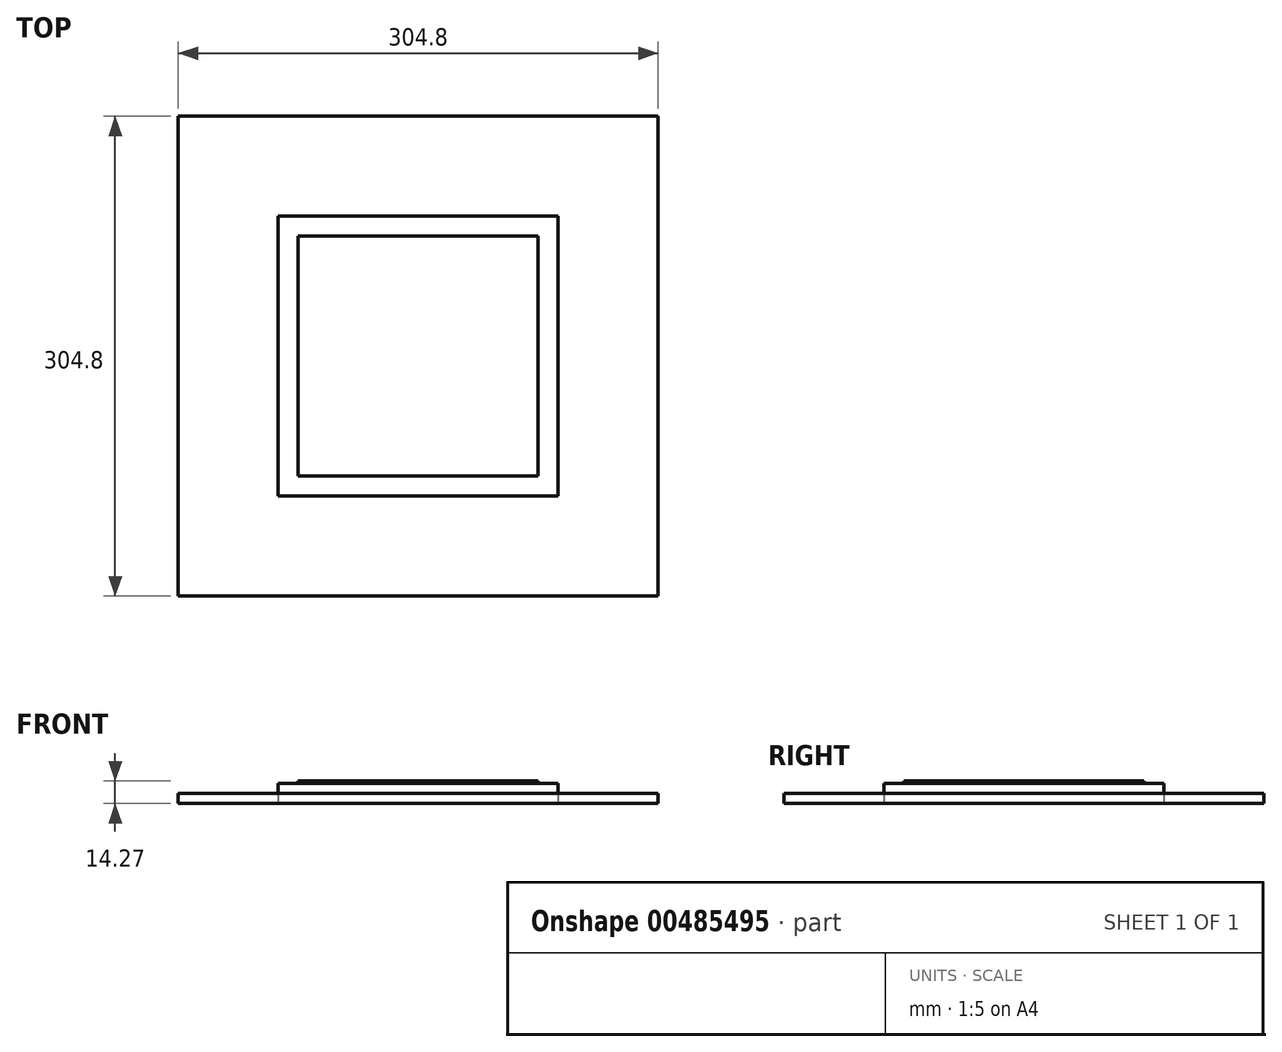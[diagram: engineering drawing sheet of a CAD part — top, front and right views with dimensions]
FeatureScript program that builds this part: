
annotation { "Feature Type Name" : "Feature", "Feature Type Description" : "" }
export const myFeature = defineFeature(function(context is Context, id is Id, definition is map)
    precondition{}
    {
        {
            var Q0;
            Q0=qCreatedBy(makeId("Top.planeOp"),FACE);
            var sketch = newSketch(context, id + "F0", { "sketchPlane" : qUnion([Q0])});
            skLineSegment(sketch, "E0.bottom", {"start": v(152.4, 152.4) * mm, "end": v(-152.4, 152.4) * mm});
            skLineSegment(sketch, "E0.top", {"start": v(152.4, -152.4) * mm, "end": v(-152.4, -152.4) * mm});
            skLineSegment(sketch, "E0.left", {"start": v(152.4, 152.4) * mm, "end": v(152.4, -152.4) * mm});
            skLineSegment(sketch, "E0.right", {"start": v(-152.4, 152.4) * mm, "end": v(-152.4, -152.4) * mm});
            skPoint(sketch, "E0.middle", {"position": v(0, 0) * mm});
            skSolve(sketch);
        }
        {
            var Q0;
            Q0=makeQuery(id+"F0.imprint","IMPRINT",FACE,{"disambiguationData":[TD([[makeQuery(id+"F0.imprint","IMPRINT",EDGE,{"derivedFrom":sQuery(id+"F0.wireOp",EDGE,"E0.bottom")}),1.0]])]});
            extrude(context, id + "F1", {"entities" : qUnion([Q0]), "depth" : 6.35 * mm});
        }
        {
            var Q0;
            Q0=qCreatedBy(makeId("Top.planeOp"),FACE);
            var sketch = newSketch(context, id + "F2", { "sketchPlane" : qUnion([Q0])});
            skLineSegment(sketch, "E1.bottom", {"start": v(88.9, 88.9) * mm, "end": v(-88.9, 88.9) * mm});
            skLineSegment(sketch, "E1.top", {"start": v(88.9, -88.9) * mm, "end": v(-88.9, -88.9) * mm});
            skLineSegment(sketch, "E1.left", {"start": v(88.9, 88.9) * mm, "end": v(88.9, -88.9) * mm});
            skLineSegment(sketch, "E1.right", {"start": v(-88.9, 88.9) * mm, "end": v(-88.9, -88.9) * mm});
            skPoint(sketch, "E1.middle", {"position": v(0, 0) * mm});
            skSolve(sketch);
        }
        {
            var Q0;
            Q0=makeQuery(id+"F2.imprint","IMPRINT",FACE,{"disambiguationData":[TD([[makeQuery(id+"F2.imprint","IMPRINT",EDGE,{"derivedFrom":sQuery(id+"F2.wireOp",EDGE,"E1.bottom")}),1.0]])]});
            extrude(context, id + "F3", {"entities" : qUnion([Q0]), "depth" : 12.7 * mm});
        }
        {
            var Q0;
            Q0=makeQuery(id+"F3.opExtrude","CAP_FACE",FACE,{"disambiguationData":[OSD([sQuery(id+"F2.wireOp",EDGE,"E1.bottom"),sQuery(id+"F2.wireOp",EDGE,"E1.top"),sQuery(id+"F2.wireOp",EDGE,"E1.left"),sQuery(id+"F2.wireOp",EDGE,"E1.right")])],"isStart":false});
            var sketch = newSketch(context, id + "F4", { "sketchPlane" : qUnion([Q0])});
            skLineSegment(sketch, "E2.bottom", {"start": v(76.2, -76.2) * mm, "end": v(-76.2, -76.2) * mm});
            skLineSegment(sketch, "E2.top", {"start": v(76.2, 76.2) * mm, "end": v(-76.2, 76.2) * mm});
            skLineSegment(sketch, "E2.left", {"start": v(76.2, -76.2) * mm, "end": v(76.2, 76.2) * mm});
            skLineSegment(sketch, "E2.right", {"start": v(-76.2, -76.2) * mm, "end": v(-76.2, 76.2) * mm});
            skPoint(sketch, "E2.middle", {"position": v(0, 0) * mm});
            skSolve(sketch);
        }
        {
            var Q0;
            Q0=makeQuery(id+"F4.imprint","IMPRINT",FACE,{"disambiguationData":[TD([[makeQuery(id+"F4.imprint","IMPRINT",EDGE,{"derivedFrom":sQuery(id+"F4.wireOp",EDGE,"E2.bottom")}),-1.0]])]});
            extrude(context, id + "F5", {"entities" : qUnion([Q0]), "depth" : 1.57 * mm});
        }
    });
